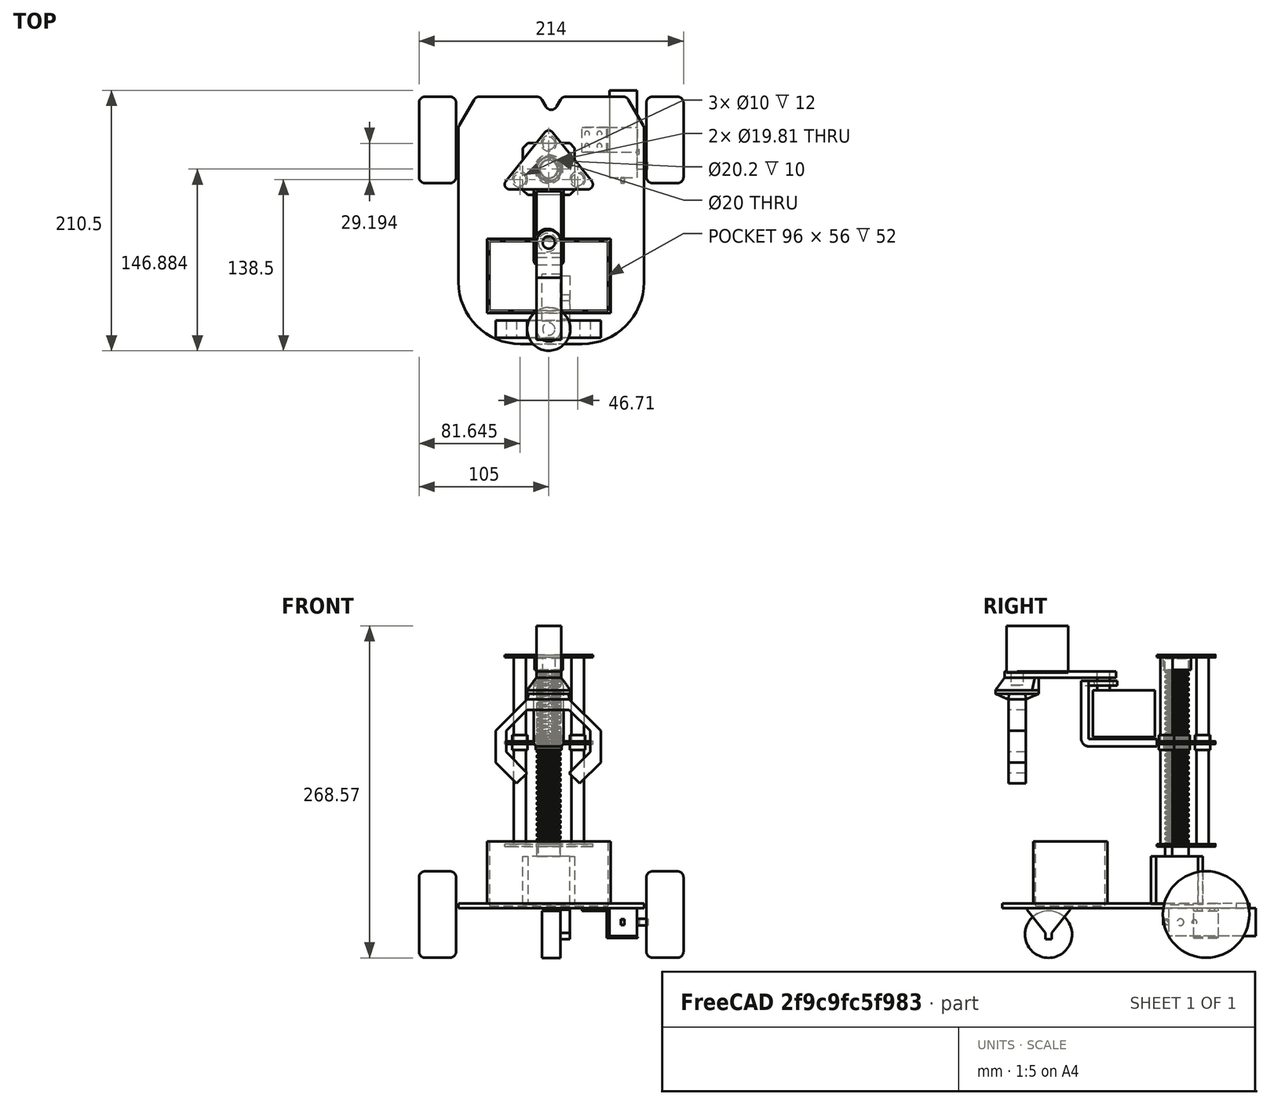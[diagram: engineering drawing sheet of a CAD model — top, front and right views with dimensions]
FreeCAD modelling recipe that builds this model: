
FCSTD DOCUMENT  (FreeCAD 0.19R24291 (Git))
Label: motor_chasis_union
License: All rights reserved
LicenseURL: http://en.wikipedia.org/wiki/All_rights_reserved
objects: Part::Feature×11, Part::Box×5, Part::MultiFuse×5, Part::Cylinder×4, App::Link×3, Part::Cut×2, Part::Compound2×1
note: 27 computed .brp shape members not serialized (recipe doc carries the construction recipe); baked Part::Feature solids carry a one-line shape summary decoded from their .brp

FEATURE [Part::Feature] Solid
  shape: bbox 42 x 42 x 199 mm, 88 faces (baked)
FEATURE [Part::Feature] Solid001
  shape: bbox 30 x 75.77 x 75.77 mm, 5 faces (baked)
FEATURE [Part::Feature] Solid002
  shape: bbox 30 x 75.77 x 75.77 mm, 5 faces (baked)
FEATURE [Part::Feature] Solid003
  shape: bbox 150 x 200 x 54 mm, 30 faces (baked)
FEATURE [Part::Feature] Solid004
  shape: bbox 22.5 x 38 x 40.07 mm, 13 faces (baked)
FEATURE [Part::Feature] Solid005
  shape: bbox 71.36 x 47.6 x 155 mm, 24 faces (baked)
FEATURE [Part::Feature] Solid006
  shape: bbox 71.36 x 47.6 x 13.26 mm, 37 faces (baked)
FEATURE [Part::Feature] Solid007
  shape: bbox 20 x 50 x 53 mm, 8 faces (baked)
FEATURE [Part::Feature] Solid008
  shape: bbox 20 x 50 x 48 mm, 8 faces (baked)
FEATURE [Part::Feature] Solid009
  shape: bbox 24 x 61 x 53 mm, 18 faces (baked)
FEATURE [Part::Feature] Solid010
  shape: bbox 85 x 97.5 x 90.5 mm, 32 faces (baked)
FEATURE [Part::Compound2] Compound  label="Simulacion - 1 v2"
  Links = -> [Solid,Solid001,Solid002,Solid003,Solid004,Solid005,Solid006,Solid007,Solid008,Solid009,Solid010]
FEATURE [Part::Box] Box  label="Base"
  AttacherType = Attacher::AttachEngine3D
  Height = 22.4
  Length = 70.4
  Width = 22.44
FEATURE [Part::Box] Box001  label="Cube001"
  AttacherType = Attacher::AttachEngine3D
  Height = 2.8
  Length = 4.8
  Placement = pos=(70,8.66,9.3) rot=(0,0,1;0rad)
  Width = 5
FEATURE [Part::Cylinder] Cylinder
  Angle = 360
  AttacherType = Attacher::AttachEngine3D
  Height = 10
  Placement = pos=(72.4,11.22,8.3) rot=(0,0,1;0rad)
  Radius = 1.5
FEATURE [Part::Cut] Cut  label="anclaje"
  Base = -> Box001
  Refine = true
  Tool = -> Cylinder
FEATURE [Part::MultiFuse] Fusion
  Refine = true
  Shapes = -> [Cut,Box]
FEATURE [Part::Cylinder] Cylinder001
  Angle = 360
  AttacherType = Attacher::AttachEngine3D
  Height = 8.7
  Placement = pos=(60.75,11.22,22.44) rot=(0,0,1;0rad)
  Radius = 2.7
FEATURE [Part::MultiFuse] Fusion001
  Refine = true
  Shapes = -> [Cylinder001,Fusion]
FEATURE [Part::Cylinder] Cylinder002
  Angle = 360
  AttacherType = Attacher::AttachEngine3D
  Height = 1.92
  Placement = pos=(49.5,11.22,22.44) rot=(0,0,1;0rad)
  Radius = 2
FEATURE [Part::MultiFuse] Fusion002  label="Motor"
  Placement = pos=(289,70,-50) rot=(-0.57735,0.57735,-0.57735;2.0944rad)
  Refine = true
  Shapes = -> [Cylinder002,Fusion001]
FEATURE [Part::Box] Box002  label="s_lateral"
  AttacherType = Attacher::AttachEngine3D
  Height = 23
  Length = 20
  Placement = pos=(288,20,-73) rot=(0,0,1;1.5708rad)
  Width = 1
FEATURE [Part::Box] Box003  label="s_abajo"
  AttacherType = Attacher::AttachEngine3D
  Height = 1
  Length = 25
  Placement = pos=(287,20,-74) rot=(0,0,1;0rad)
  Width = 20
FEATURE [Part::Box] Box004  label="s_arriba"
  AttacherType = Attacher::AttachEngine3D
  Height = 2
  Length = 20
  Placement = pos=(267,20,-52) rot=(0,0,1;0rad)
  Width = 20
FEATURE [Part::MultiFuse] Fusion003
  Placement = pos=(-288,-20,73) rot=(0,0,1;0rad)
  Refine = true
  Shapes = -> [Box004,Box003,Box002]
FEATURE [Part::Cylinder] Cylinder003
  Angle = 360
  AttacherType = Attacher::AttachEngine3D
  Height = 10
  Placement = pos=(-7,5,20) rot=(0,0,1;0rad)
  Radius = 2
FEATURE [App::Link] Link  label="Cylinder004"
  LinkPlacement = pos=(-17,5,20) rot=(0,0,1;0rad)
  LinkedObject = -> Cylinder003
  Placement = pos=(-17,5,20) rot=(0,0,1;0rad)
FEATURE [App::Link] Link001  label="Cylinder005"
  LinkPlacement = pos=(-17,15,20) rot=(0,0,1;0rad)
  LinkedObject = -> Cylinder003
  Placement = pos=(-17,15,20) rot=(0,0,1;0rad)
FEATURE [App::Link] Link002  label="Cylinder006"
  LinkPlacement = pos=(-7,15,20) rot=(0,0,1;0rad)
  LinkedObject = -> Cylinder003
  Placement = pos=(-7,15,20) rot=(0,0,1;0rad)
FEATURE [Part::MultiFuse] Fusion004
  Refine = true
  Shapes = -> [Cylinder003,Link,Link001,Link002]
FEATURE [Part::Cut] Cut001  label="soporte"
  Base = -> Fusion003
  Placement = pos=(288,20,-73) rot=(0,0,1;0rad)
  Refine = true
  Tool = -> Fusion004
